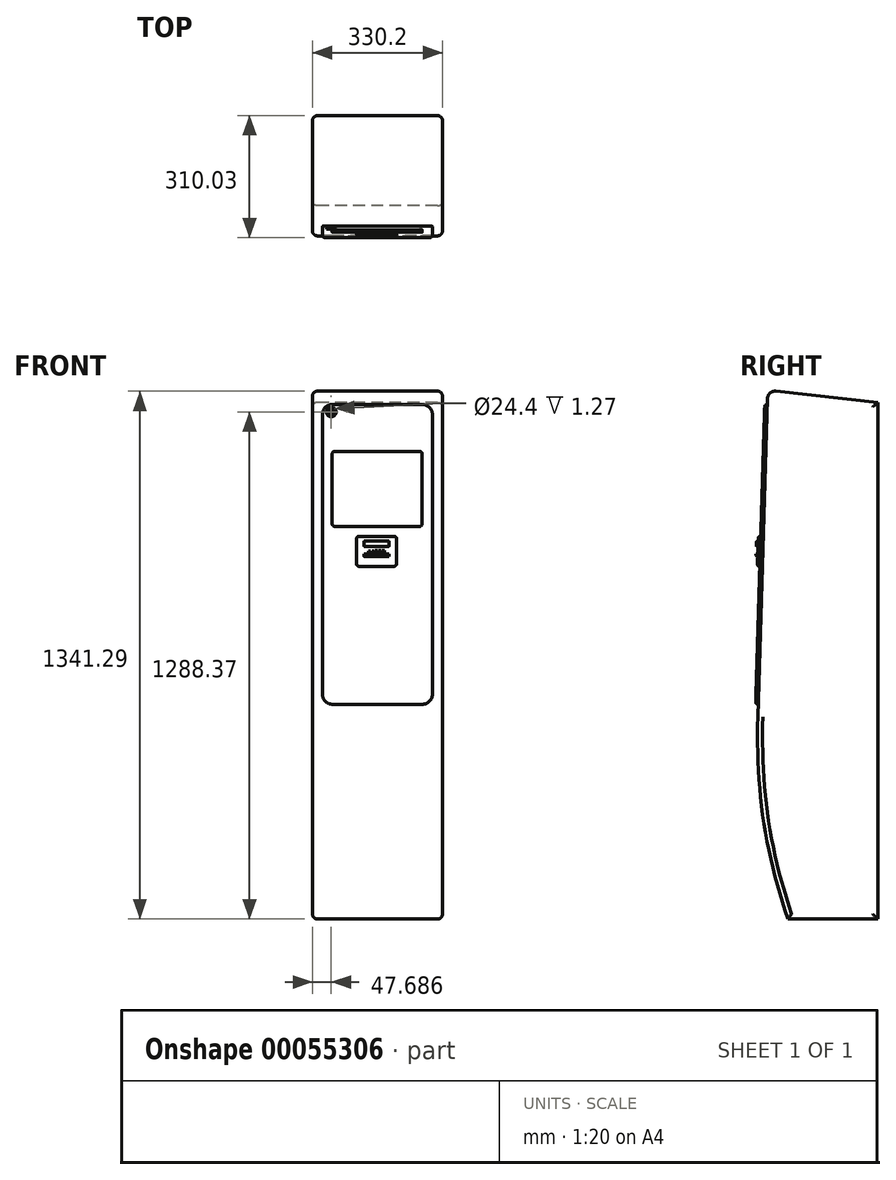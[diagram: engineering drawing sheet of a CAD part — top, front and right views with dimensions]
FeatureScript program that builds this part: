
annotation { "Feature Type Name" : "Feature", "Feature Type Description" : "" }
export const myFeature = defineFeature(function(context is Context, id is Id, definition is map)
    precondition{}
    {
        {
            var Q0;
            Q0=qCreatedBy(makeId("Right.planeOp"),FACE);
            var sketch = newSketch(context, id + "F0", { "sketchPlane" : qUnion([Q0])});
            skLineSegment(sketch, "E0", {"start": v(190.43, -816.62) * mm, "end": v(-38.17, -816.62) * mm});
            skLineSegment(sketch, "E1", {"start": v(190.26, 496.2) * mm, "end": v(190.43, -816.62) * mm});
            skPoint(sketch, "E2.visualSharp", {"position": v(190.26, 519.4) * mm});
            skLineSegment(sketch, "E3", {"start": v(-68.57, 524.56) * mm, "end": v(190.26, 496.2) * mm});
            skLineSegment(sketch, "E4", {"start": v(190.43, -816.62) * mm, "end": v(190.37, -308.62) * mm});
            skFitSpline(sketch, "E5", {"points": [v(-114.37, -302.53) * mm, v(-38.17, -816.62) * mm], "startDerivative": vector(-16.58, -646.57) * mm, "endDerivative": vector(152.32, -464.69) * mm});
            skLineSegment(sketch, "E6", {"start": v(-114.37, -302.47) * mm, "end": v(-89.68, 506.2) * mm});
            skPoint(sketch, "E7.orphan", {"position": v(-114.37, 529.58) * mm});
            skArc(sketch, "E8.filletArc", {"start": v(-114.37, -302.47) * mm, "mid": v(-114.37, -302.53) * mm, "end": v(-114.37, -302.59) * mm});
            skPoint(sketch, "E9.visualSharp", {"position": v(-89.05, 526.8) * mm});
            skArc(sketch, "E9.filletArc", {"start": v(-68.57, 524.56) * mm, "mid": v(-83.14, 520) * mm, "end": v(-89.68, 506.2) * mm});
            skSolve(sketch);
        }
        {
            var Q0;
            Q0=makeQuery(id+"F0.imprint","IMPRINT",FACE,{"disambiguationData":[TD([[makeQuery(id+"F0.imprint","IMPRINT",EDGE,{"derivedFrom":sQuery(id+"F0.wireOp",EDGE,"E0")}),-1.0]])]});
            extrude(context, id + "F1", {"entities" : qUnion([Q0]), "depth" : 330.2 * mm});
        }
        {
            var Q0;
            Q0=makeQuery(id+"F1.opExtrude","SWEPT_FACE",FACE,{"disambiguationData":[OSD([sQuery(id+"F0.wireOp",EDGE,"E6")])]});
            var sketch = newSketch(context, id + "F2", { "sketchPlane" : qUnion([Q0])});
            skLineSegment(sketch, "E10.bottom", {"start": v(50.64, 487.78) * mm, "end": v(279.24, 487.78) * mm});
            skLineSegment(sketch, "E10.top", {"start": v(50.64, -274.22) * mm, "end": v(279.24, -274.22) * mm});
            skLineSegment(sketch, "E10.left", {"start": v(25.24, 462.38) * mm, "end": v(25.24, -248.82) * mm});
            skLineSegment(sketch, "E10.right", {"start": v(304.64, 462.38) * mm, "end": v(304.64, -248.82) * mm});
            skPoint(sketch, "E11.visualSharp", {"position": v(25.24, 487.78) * mm});
            skArc(sketch, "E11.filletArc", {"start": v(50.64, 487.78) * mm, "mid": v(32.68, 480.34) * mm, "end": v(25.24, 462.38) * mm});
            skPoint(sketch, "E12.visualSharp", {"position": v(25.24, -274.22) * mm});
            skArc(sketch, "E12.filletArc", {"start": v(25.24, -248.82) * mm, "mid": v(32.68, -266.78) * mm, "end": v(50.64, -274.22) * mm});
            skPoint(sketch, "E13.visualSharp", {"position": v(304.64, -274.22) * mm});
            skArc(sketch, "E13.filletArc", {"start": v(279.24, -274.22) * mm, "mid": v(297.2, -266.78) * mm, "end": v(304.64, -248.82) * mm});
            skPoint(sketch, "E14.visualSharp", {"position": v(304.64, 487.78) * mm});
            skArc(sketch, "E14.filletArc", {"start": v(304.64, 462.38) * mm, "mid": v(297.2, 480.34) * mm, "end": v(279.24, 487.78) * mm});
            skSolve(sketch);
        }
        {
            var Q0;
            Q0 = qSketchRegion(id + "F2", true);
            extrude(context, id + "F3", {"entities" : qUnion([Q0]), "operationType" : NewBodyOperationType.ADD, "depth" : 6.35 * mm});
        }
        {
            var Q0;
            Q0=makeQuery(id+"F3.opExtrude","CAP_EDGE",EDGE,{"disambiguationData":[OSD([sQuery(id+"F2.wireOp",EDGE,"E10.bottom")])],"isStart":false});
            var Q1;
            Q1=makeQuery(id+"F3.opExtrude","CAP_EDGE",EDGE,{"disambiguationData":[OSD([sQuery(id+"F2.wireOp",EDGE,"E10.right")])],"isStart":false});
            var Q2;
            Q2=makeQuery(id+"F3.opExtrude","CAP_EDGE",EDGE,{"disambiguationData":[OSD([sQuery(id+"F2.wireOp",EDGE,"E10.top")])],"isStart":false});
            var Q3;
            Q3=makeQuery(id+"F3.opExtrude","CAP_EDGE",EDGE,{"disambiguationData":[OSD([sQuery(id+"F2.wireOp",EDGE,"E12.filletArc")])],"isStart":false});
            var Q4;
            Q4=makeQuery(id+"F3.opExtrude","CAP_EDGE",EDGE,{"disambiguationData":[OSD([sQuery(id+"F2.wireOp",EDGE,"E13.filletArc")])],"isStart":false});
            var Q5;
            Q5=makeQuery(id+"F3.opExtrude","CAP_EDGE",EDGE,{"disambiguationData":[OSD([sQuery(id+"F2.wireOp",EDGE,"E14.filletArc")])],"isStart":false});
            var Q6;
            Q6=makeQuery(id+"F3.opExtrude","CAP_EDGE",EDGE,{"disambiguationData":[OSD([sQuery(id+"F2.wireOp",EDGE,"E11.filletArc")])],"isStart":false});
            var Q7;
            Q7=makeQuery(id+"F3.opExtrude","CAP_FACE",FACE,{"disambiguationData":[OSD([sQuery(id+"F2.wireOp",EDGE,"E10.bottom"),sQuery(id+"F2.wireOp",EDGE,"E10.top"),sQuery(id+"F2.wireOp",EDGE,"E10.left"),sQuery(id+"F2.wireOp",EDGE,"E10.right"),sQuery(id+"F2.wireOp",EDGE,"E11.filletArc"),sQuery(id+"F2.wireOp",EDGE,"E12.filletArc"),sQuery(id+"F2.wireOp",EDGE,"E13.filletArc"),sQuery(id+"F2.wireOp",EDGE,"E14.filletArc")])],"isStart":false});
            var Q8;
            Q8=makeQuery(id+"F3.opExtrude","CAP_EDGE",EDGE,{"disambiguationData":[OSD([sQuery(id+"F2.wireOp",EDGE,"E10.left")])],"isStart":false});
            fillet(context, id + "F4", {"entities" : qUnion([Q0, Q1, Q2, Q3, Q4, Q5, Q6, Q7, Q8]), "radius" : 5.08 * mm, "tangentPropagation" : true, "allowEdgeOverflow" : false});
        }
        {
            var Q0;
            Q0=makeQuery(id+"F3.opExtrude","CAP_FACE",FACE,{"disambiguationData":[OSD([sQuery(id+"F2.wireOp",EDGE,"E10.bottom"),sQuery(id+"F2.wireOp",EDGE,"E10.top"),sQuery(id+"F2.wireOp",EDGE,"E10.left"),sQuery(id+"F2.wireOp",EDGE,"E10.right"),sQuery(id+"F2.wireOp",EDGE,"E11.filletArc"),sQuery(id+"F2.wireOp",EDGE,"E12.filletArc"),sQuery(id+"F2.wireOp",EDGE,"E13.filletArc"),sQuery(id+"F2.wireOp",EDGE,"E14.filletArc")])],"isStart":false});
            var sketch = newSketch(context, id + "F5", { "sketchPlane" : qUnion([Q0])});
            skLineSegment(sketch, "E15", {"start": v(56.4, 368.4) * mm, "end": v(272.3, 368.4) * mm});
            skLineSegment(sketch, "E16", {"start": v(50.04, 362.05) * mm, "end": v(50.04, 184.25) * mm});
            skLineSegment(sketch, "E17", {"start": v(56.4, 177.9) * mm, "end": v(272.3, 177.9) * mm});
            skLineSegment(sketch, "E18", {"start": v(278.64, 184.25) * mm, "end": v(278.64, 362.05) * mm});
            skLineSegment(sketch, "E19.bottom", {"start": v(118.32, 152.5) * mm, "end": v(207.22, 152.5) * mm});
            skLineSegment(sketch, "E19.top", {"start": v(118.32, 76.3) * mm, "end": v(207.22, 76.3) * mm});
            skLineSegment(sketch, "E19.left", {"start": v(111.97, 146.15) * mm, "end": v(111.97, 82.65) * mm});
            skLineSegment(sketch, "E19.right", {"start": v(213.57, 146.15) * mm, "end": v(213.57, 82.65) * mm});
            skPoint(sketch, "E20.visualSharp", {"position": v(50.04, 368.4) * mm});
            skArc(sketch, "E20.filletArc", {"start": v(56.4, 368.4) * mm, "mid": v(51.9, 366.54) * mm, "end": v(50.04, 362.05) * mm});
            skPoint(sketch, "E21.visualSharp", {"position": v(278.64, 368.4) * mm});
            skArc(sketch, "E21.filletArc", {"start": v(278.64, 362.05) * mm, "mid": v(276.78, 366.54) * mm, "end": v(272.3, 368.4) * mm});
            skPoint(sketch, "E22.visualSharp", {"position": v(278.64, 177.9) * mm});
            skArc(sketch, "E22.filletArc", {"start": v(272.3, 177.9) * mm, "mid": v(276.78, 179.76) * mm, "end": v(278.64, 184.25) * mm});
            skPoint(sketch, "E23.visualSharp", {"position": v(50.04, 177.9) * mm});
            skArc(sketch, "E23.filletArc", {"start": v(50.04, 184.25) * mm, "mid": v(51.9, 179.76) * mm, "end": v(56.4, 177.9) * mm});
            skPoint(sketch, "E24.visualSharp", {"position": v(111.97, 152.5) * mm});
            skArc(sketch, "E24.filletArc", {"start": v(118.32, 152.5) * mm, "mid": v(113.83, 150.64) * mm, "end": v(111.97, 146.15) * mm});
            skPoint(sketch, "E25.visualSharp", {"position": v(213.57, 152.5) * mm});
            skArc(sketch, "E25.filletArc", {"start": v(213.57, 146.15) * mm, "mid": v(211.71, 150.64) * mm, "end": v(207.22, 152.5) * mm});
            skPoint(sketch, "E26.visualSharp", {"position": v(213.57, 76.3) * mm});
            skArc(sketch, "E26.filletArc", {"start": v(207.22, 76.3) * mm, "mid": v(211.71, 78.16) * mm, "end": v(213.57, 82.65) * mm});
            skPoint(sketch, "E27.visualSharp", {"position": v(111.97, 76.3) * mm});
            skArc(sketch, "E27.filletArc", {"start": v(111.97, 82.65) * mm, "mid": v(113.83, 78.16) * mm, "end": v(118.32, 76.3) * mm});
            skSolve(sketch);
        }
        {
            var Q0;
            Q0=makeQuery(id+"F5.imprint","IMPRINT",FACE,{"disambiguationData":[TD([[makeQuery(id+"F5.imprint","IMPRINT",EDGE,{"derivedFrom":sQuery(id+"F5.wireOp",EDGE,"E15")}),-1.0]])]});
            extrude(context, id + "F6", {"entities" : qUnion([Q0]), "operationType" : NewBodyOperationType.REMOVE, "oppositeDirection" : true, "depth" : 2.54 * mm});
        }
        {
            var Q0;
            Q0=makeQuery(id+"F5.imprint","IMPRINT",FACE,{"disambiguationData":[TD([[makeQuery(id+"F5.imprint","IMPRINT",EDGE,{"derivedFrom":sQuery(id+"F5.wireOp",EDGE,"E19.bottom")}),-1.0]])]});
            extrude(context, id + "F7", {"entities" : qUnion([Q0]), "operationType" : NewBodyOperationType.ADD, "depth" : 6.35 * mm});
        }
        {
            var Q0;
            Q0=makeQuery(id+"F7.opExtrude","CAP_FACE",FACE,{"disambiguationData":[OSD([sQuery(id+"F5.wireOp",EDGE,"E19.bottom"),sQuery(id+"F5.wireOp",EDGE,"E19.top"),sQuery(id+"F5.wireOp",EDGE,"E19.left"),sQuery(id+"F5.wireOp",EDGE,"E19.right"),sQuery(id+"F5.wireOp",EDGE,"E24.filletArc"),sQuery(id+"F5.wireOp",EDGE,"E25.filletArc"),sQuery(id+"F5.wireOp",EDGE,"E26.filletArc"),sQuery(id+"F5.wireOp",EDGE,"E27.filletArc")])],"isStart":false});
            fillet(context, id + "F8", {"entities" : qUnion([Q0]), "radius" : 5.08 * mm, "tangentPropagation" : true, "allowEdgeOverflow" : false});
        }
        {
            var Q0;
            Q0=makeQuery(id+"F7.opExtrude","CAP_FACE",FACE,{"disambiguationData":[OSD([sQuery(id+"F5.wireOp",EDGE,"E19.bottom"),sQuery(id+"F5.wireOp",EDGE,"E19.top"),sQuery(id+"F5.wireOp",EDGE,"E19.left"),sQuery(id+"F5.wireOp",EDGE,"E19.right"),sQuery(id+"F5.wireOp",EDGE,"E24.filletArc"),sQuery(id+"F5.wireOp",EDGE,"E25.filletArc"),sQuery(id+"F5.wireOp",EDGE,"E26.filletArc"),sQuery(id+"F5.wireOp",EDGE,"E27.filletArc")])],"isStart":false});
            var sketch = newSketch(context, id + "F9", { "sketchPlane" : qUnion([Q0])});
            skLineSegment(sketch, "E28", {"start": v(131.13, 107.36) * mm, "end": v(194.63, 107.36) * mm});
            skLineSegment(sketch, "E29", {"start": v(131.13, 101.01) * mm, "end": v(194.63, 101.01) * mm});
            skLineSegment(sketch, "E30", {"start": v(194.63, 101.01) * mm, "end": v(194.63, 107.36) * mm});
            skLineSegment(sketch, "E31", {"start": v(131.13, 107.36) * mm, "end": v(131.13, 101.01) * mm});
            skPoint(sketch, "E32.startSnap0", {"position": v(131.13, 104.19) * mm});
            skLineSegment(sketch, "E33.bottom", {"start": v(132.05, 106.34) * mm, "end": v(193.6, 106.34) * mm});
            skLineSegment(sketch, "E33.top", {"start": v(132.05, 101.87) * mm, "end": v(193.6, 101.87) * mm});
            skLineSegment(sketch, "E33.left", {"start": v(132.05, 106.34) * mm, "end": v(132.05, 101.87) * mm});
            skLineSegment(sketch, "E33.right", {"start": v(193.6, 106.34) * mm, "end": v(193.6, 101.87) * mm});
            skSolve(sketch);
        }
        {
            var Q0;
            Q0=makeQuery(id+"F9.imprint","IMPRINT",FACE,{"disambiguationData":[TD([[makeQuery(id+"F9.imprint","IMPRINT",EDGE,{"derivedFrom":sQuery(id+"F9.wireOp",EDGE,"E28")}),-1.0]])]});
            extrude(context, id + "F10", {"entities" : qUnion([Q0]), "operationType" : NewBodyOperationType.ADD, "depth" : 5.08 * mm});
        }
        {
            var Q0;
            Q0=makeQuery(id+"F10.opExtrude","CAP_EDGE",EDGE,{"disambiguationData":[OSD([sQuery(id+"F9.wireOp",EDGE,"E29")])],"isStart":false});
            fillet(context, id + "F11", {"entities" : qUnion([Q0]), "radius" : 5.08 * mm, "tangentPropagation" : true, "allowEdgeOverflow" : false});
        }
        {
            var Q0;
            {var subQ0=sQuery(id+"F5.wireOp",EDGE,"E24.filletArc");var subQ1=sQuery(id+"F5.wireOp",EDGE,"E19.bottom");var subQ2=sQuery(id+"F5.wireOp",EDGE,"E27.filletArc");var subQ3=sQuery(id+"F5.wireOp",EDGE,"E26.filletArc");var subQ4=sQuery(id+"F5.wireOp",EDGE,"E25.filletArc");var subQ5=sQuery(id+"F5.wireOp",EDGE,"E19.top");var subQ6=sQuery(id+"F5.wireOp",EDGE,"E19.left");var subQ7=sQuery(id+"F5.wireOp",EDGE,"E19.right");Q0=makeQuery(id+"F10.boolean.opBoolean","SPLIT",FACE,{"disambiguationData":[TD([makeQuery(id+"F8.opFillet","BLEND_FACE",FACE,{"disambiguationData":[OSD([subQ1])]})])],"derivedFrom":makeQuery(id+"F7.opExtrude","CAP_FACE",FACE,{"disambiguationData":[OSD([subQ1,subQ5,subQ6,subQ7,subQ0,subQ4,subQ3,subQ2])],"isStart":false})});}
            var sketch = newSketch(context, id + "F12", { "sketchPlane" : qUnion([Q0])});
            skLineSegment(sketch, "E34.bottom", {"start": v(142.12, 115.26) * mm, "end": v(147.6, 115.26) * mm});
            skLineSegment(sketch, "E34.top", {"start": v(142.12, 109.78) * mm, "end": v(147.6, 109.78) * mm});
            skLineSegment(sketch, "E34.left", {"start": v(142.12, 115.26) * mm, "end": v(142.12, 109.78) * mm});
            skLineSegment(sketch, "E34.right", {"start": v(147.6, 115.26) * mm, "end": v(147.6, 109.78) * mm});
            skLineSegment(sketch, "E35.bottom", {"start": v(150.79, 115.26) * mm, "end": v(156.72, 115.26) * mm});
            skLineSegment(sketch, "E35.top", {"start": v(150.79, 109.78) * mm, "end": v(156.72, 109.78) * mm});
            skLineSegment(sketch, "E35.left", {"start": v(150.79, 115.26) * mm, "end": v(150.79, 109.78) * mm});
            skLineSegment(sketch, "E35.right", {"start": v(156.72, 115.26) * mm, "end": v(156.72, 109.78) * mm});
            skLineSegment(sketch, "E36.bottom", {"start": v(159.46, 115.72) * mm, "end": v(165.16, 115.72) * mm});
            skLineSegment(sketch, "E36.top", {"start": v(159.46, 110) * mm, "end": v(165.16, 110) * mm});
            skLineSegment(sketch, "E36.left", {"start": v(159.46, 115.72) * mm, "end": v(159.46, 110) * mm});
            skLineSegment(sketch, "E36.right", {"start": v(165.16, 115.72) * mm, "end": v(165.16, 110) * mm});
            skLineSegment(sketch, "E37.bottom", {"start": v(168.13, 115.72) * mm, "end": v(173.6, 115.72) * mm});
            skLineSegment(sketch, "E37.top", {"start": v(168.13, 110.24) * mm, "end": v(173.6, 110.24) * mm});
            skLineSegment(sketch, "E37.left", {"start": v(168.13, 115.72) * mm, "end": v(168.13, 110.24) * mm});
            skLineSegment(sketch, "E37.right", {"start": v(173.6, 115.72) * mm, "end": v(173.6, 110.24) * mm});
            skLineSegment(sketch, "E38.bottom", {"start": v(176.34, 115.72) * mm, "end": v(182.5, 115.72) * mm});
            skLineSegment(sketch, "E38.top", {"start": v(176.34, 110) * mm, "end": v(182.5, 110) * mm});
            skLineSegment(sketch, "E38.left", {"start": v(176.34, 115.72) * mm, "end": v(176.34, 110) * mm});
            skLineSegment(sketch, "E38.right", {"start": v(182.5, 115.72) * mm, "end": v(182.5, 110) * mm});
            skSolve(sketch);
        }
        {
            var Q0;
            Q0 = qSketchRegion(id + "F12", true);
            extrude(context, id + "F13", {"entities" : qUnion([Q0]), "operationType" : NewBodyOperationType.REMOVE, "oppositeDirection" : true, "depth" : 1.27 * mm});
        }
        {
            var Q0;
            Q0=makeQuery(id+"F5.imprint","IMPRINT",FACE,{"disambiguationData":[TD([[makeQuery(id+"F5.imprint","IMPRINT",EDGE,{"derivedFrom":sQuery(id+"F5.wireOp",EDGE,"E15")}),1.0]])]});
            var sketch = newSketch(context, id + "F14", { "sketchPlane" : qUnion([Q0])});
            skCircle(sketch, "E39", {"center": v(47.69, 468.59) * mm, "radius": 12.2 * mm});
            skArc(sketch, "E40", {"start": v(47.69, 479.73) * mm, "mid": v(40.2, 460.46) * mm, "end": v(59.21, 468.59) * mm});
            skArc(sketch, "E41", {"start": v(47.69, 479.03) * mm, "mid": v(40.84, 461.4) * mm, "end": v(58.33, 468.59) * mm});
            skLineSegment(sketch, "E42", {"start": v(47.69, 479.73) * mm, "end": v(47.69, 479.03) * mm});
            skLineSegment(sketch, "E43", {"start": v(58.33, 468.59) * mm, "end": v(48.8, 468.59) * mm});
            skLineSegment(sketch, "E44", {"start": v(48.8, 468.59) * mm, "end": v(48.8, 469.28) * mm});
            skLineSegment(sketch, "E45", {"start": v(48.8, 469.28) * mm, "end": v(59.14, 469.28) * mm});
            skLineSegment(sketch, "E46", {"start": v(59.14, 469.28) * mm, "end": v(59.21, 468.59) * mm});
            skLineSegment(sketch, "E47", {"start": v(46.75, 476.33) * mm, "end": v(46.75, 462.87) * mm});
            skLineSegment(sketch, "E48", {"start": v(46.75, 462.87) * mm, "end": v(51.24, 462.87) * mm});
            skLineSegment(sketch, "E49", {"start": v(51.24, 462.87) * mm, "end": v(51.24, 463.93) * mm});
            skLineSegment(sketch, "E50", {"start": v(51.24, 463.93) * mm, "end": v(47.74, 463.93) * mm});
            skLineSegment(sketch, "E51", {"start": v(47.74, 463.93) * mm, "end": v(47.74, 476.33) * mm});
            skCircle(sketch, "E52", {"center": v(43.38, 474.85) * mm, "radius": 1.49 * mm});
            skLineSegment(sketch, "E53", {"start": v(46.75, 476.33) * mm, "end": v(47.74, 476.33) * mm});
            skSolve(sketch);
        }
        {
            var Q0;
            Q0 = qSketchRegion(id + "F14", true);
            extrude(context, id + "F15", {"entities" : qUnion([Q0]), "operationType" : NewBodyOperationType.REMOVE, "oppositeDirection" : true, "depth" : 1.27 * mm});
        }
        {
            var Q0;
            {var subQ0=sQuery(id+"F5.wireOp",EDGE,"E24.filletArc");var subQ1=sQuery(id+"F5.wireOp",EDGE,"E19.bottom");var subQ2=sQuery(id+"F5.wireOp",EDGE,"E27.filletArc");var subQ3=sQuery(id+"F5.wireOp",EDGE,"E26.filletArc");var subQ4=sQuery(id+"F5.wireOp",EDGE,"E25.filletArc");var subQ5=sQuery(id+"F5.wireOp",EDGE,"E19.top");var subQ6=sQuery(id+"F5.wireOp",EDGE,"E19.left");var subQ7=sQuery(id+"F5.wireOp",EDGE,"E19.right");Q0=makeQuery(id+"F10.boolean.opBoolean","SPLIT",FACE,{"disambiguationData":[TD([makeQuery(id+"F8.opFillet","BLEND_FACE",FACE,{"disambiguationData":[OSD([subQ1])]})])],"derivedFrom":makeQuery(id+"F7.opExtrude","CAP_FACE",FACE,{"disambiguationData":[OSD([subQ1,subQ5,subQ6,subQ7,subQ0,subQ4,subQ3,subQ2])],"isStart":false})});}
            var sketch = newSketch(context, id + "F16", { "sketchPlane" : qUnion([Q0])});
            skLineSegment(sketch, "E54.bottom", {"start": v(132.4, 126.57) * mm, "end": v(193.36, 126.57) * mm});
            skLineSegment(sketch, "E54.top", {"start": v(132.4, 140.09) * mm, "end": v(193.36, 140.09) * mm});
            skLineSegment(sketch, "E54.left", {"start": v(131.13, 127.84) * mm, "end": v(131.13, 138.82) * mm});
            skLineSegment(sketch, "E54.right", {"start": v(194.63, 127.84) * mm, "end": v(194.63, 138.82) * mm});
            skPoint(sketch, "E55.visualSharp", {"position": v(131.13, 140.09) * mm});
            skArc(sketch, "E55.filletArc", {"start": v(132.4, 140.09) * mm, "mid": v(131.5, 139.72) * mm, "end": v(131.13, 138.82) * mm});
            skPoint(sketch, "E56.visualSharp", {"position": v(194.63, 140.09) * mm});
            skArc(sketch, "E56.filletArc", {"start": v(194.63, 138.82) * mm, "mid": v(194.25, 139.72) * mm, "end": v(193.36, 140.09) * mm});
            skPoint(sketch, "E57.visualSharp", {"position": v(194.63, 126.57) * mm});
            skArc(sketch, "E57.filletArc", {"start": v(193.36, 126.57) * mm, "mid": v(194.25, 126.94) * mm, "end": v(194.63, 127.84) * mm});
            skPoint(sketch, "E58.visualSharp", {"position": v(131.13, 126.57) * mm});
            skArc(sketch, "E58.filletArc", {"start": v(131.13, 127.84) * mm, "mid": v(131.5, 126.94) * mm, "end": v(132.4, 126.57) * mm});
            skSolve(sketch);
        }
        {
            var Q0;
            Q0 = qSketchRegion(id + "F16", true);
            extrude(context, id + "F17", {"entities" : qUnion([Q0]), "operationType" : NewBodyOperationType.ADD, "depth" : 3.8 * mm});
        }
        {
            var Q0;
            Q0=makeQuery(id+"F17.opExtrude","CAP_EDGE",EDGE,{"disambiguationData":[OSD([sQuery(id+"F16.wireOp",EDGE,"E54.right")])],"isStart":false});
            fillet(context, id + "F18", {"entities" : qUnion([Q0]), "radius" : 1.27 * mm, "tangentPropagation" : true, "allowEdgeOverflow" : false});
        }
        {
            var Q0;
            Q0=makeQuery(id+"F1.opExtrude","CAP_FACE",FACE,{"disambiguationData":[OSD([sQuery(id+"F0.wireOp",EDGE,"E0"),sQuery(id+"F0.wireOp",EDGE,"E1"),sQuery(id+"F0.wireOp",EDGE,"E3"),sQuery(id+"F0.wireOp",EDGE,"E4"),sQuery(id+"F0.wireOp",EDGE,"E5"),sQuery(id+"F0.wireOp",EDGE,"E6"),sQuery(id+"F0.wireOp",EDGE,"E8.filletArc"),sQuery(id+"F0.wireOp",EDGE,"E9.filletArc")])],"isStart":false});
            fillet(context, id + "F19", {"entities" : qUnion([Q0]), "radius" : 12.7 * mm, "tangentPropagation" : true, "allowEdgeOverflow" : false});
        }
        {
            var Q0;
            Q0=makeQuery(id+"F1.opExtrude","CAP_FACE",FACE,{"disambiguationData":[OSD([sQuery(id+"F0.wireOp",EDGE,"E0"),sQuery(id+"F0.wireOp",EDGE,"E1"),sQuery(id+"F0.wireOp",EDGE,"E3"),sQuery(id+"F0.wireOp",EDGE,"E4"),sQuery(id+"F0.wireOp",EDGE,"E5"),sQuery(id+"F0.wireOp",EDGE,"E6"),sQuery(id+"F0.wireOp",EDGE,"E8.filletArc"),sQuery(id+"F0.wireOp",EDGE,"E9.filletArc")])],"isStart":true});
            fillet(context, id + "F20", {"entities" : qUnion([Q0]), "radius" : 12.7 * mm, "tangentPropagation" : true, "allowEdgeOverflow" : false});
        }
    });
